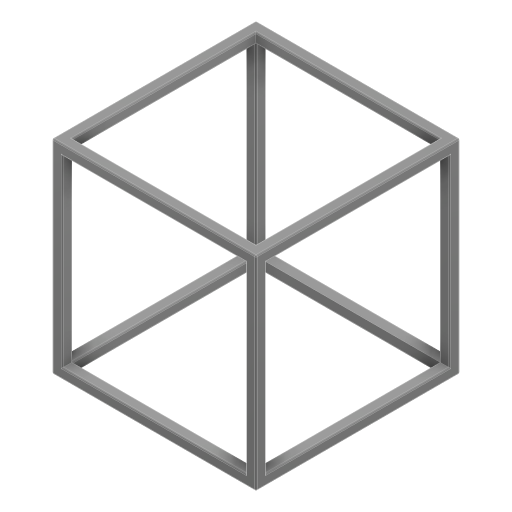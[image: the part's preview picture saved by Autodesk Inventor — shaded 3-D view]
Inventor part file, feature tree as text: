
AUTODESK INVENTOR PART (.ipt)
format: ipt  version: 2023 (Build 270158000, 158)  size: 223,744 bytes
history: native  units: in
note: dims shown in document units (in); Inventor stores cm internally (conversion verified against a paired STEP export)
features: extrude x4, sketch x4, projected_geometry x3, fillet x1
ambient origin geometry x8: Origin, YZ Plane, XZ Plane, XY Plane, X Axis, Y Axis, Z Axis, Center Point
bodies: Solid1 (feature_tree)
feature tree (12):
  extrude  "Extrusion1"  Depth=39.3701in TaperAngle=0.0deg
  extrude  "Extrusion2"  TaperAngle=0.0deg  [1 undecoded]
  extrude  "Extrusion3"  TaperAngle=0.0deg  [1 undecoded]
  extrude  "Extrusion4"  TaperAngle=0.0deg  [1 undecoded]
  fillet  "Fillet1"  Radius=0.25in
  sketch  "Sketch1"  dims[d0=39.3701in d2=39.3701in d3=0.0in]
  sketch  "Sketch2"  dims[d4=2.0in d5=0.0in d6=0.0in]
  projected_geometry  "Projected Loop1"
  sketch  "Sketch3"  dims[d7=2.0in d8=0.0in d9=0.0in]
  projected_geometry  "Projected Loop2"
  sketch  "Sketch4"  dims[d10=2.0in d11=0.0in d12=0.0in d13=0.25in]
  projected_geometry  "Projected Loop3"
note: 3 required parameter values undecoded (feature->parameter linkage not recoverable at this tier; creation-order binding heuristic only, values carry confidence <= 0.55)
